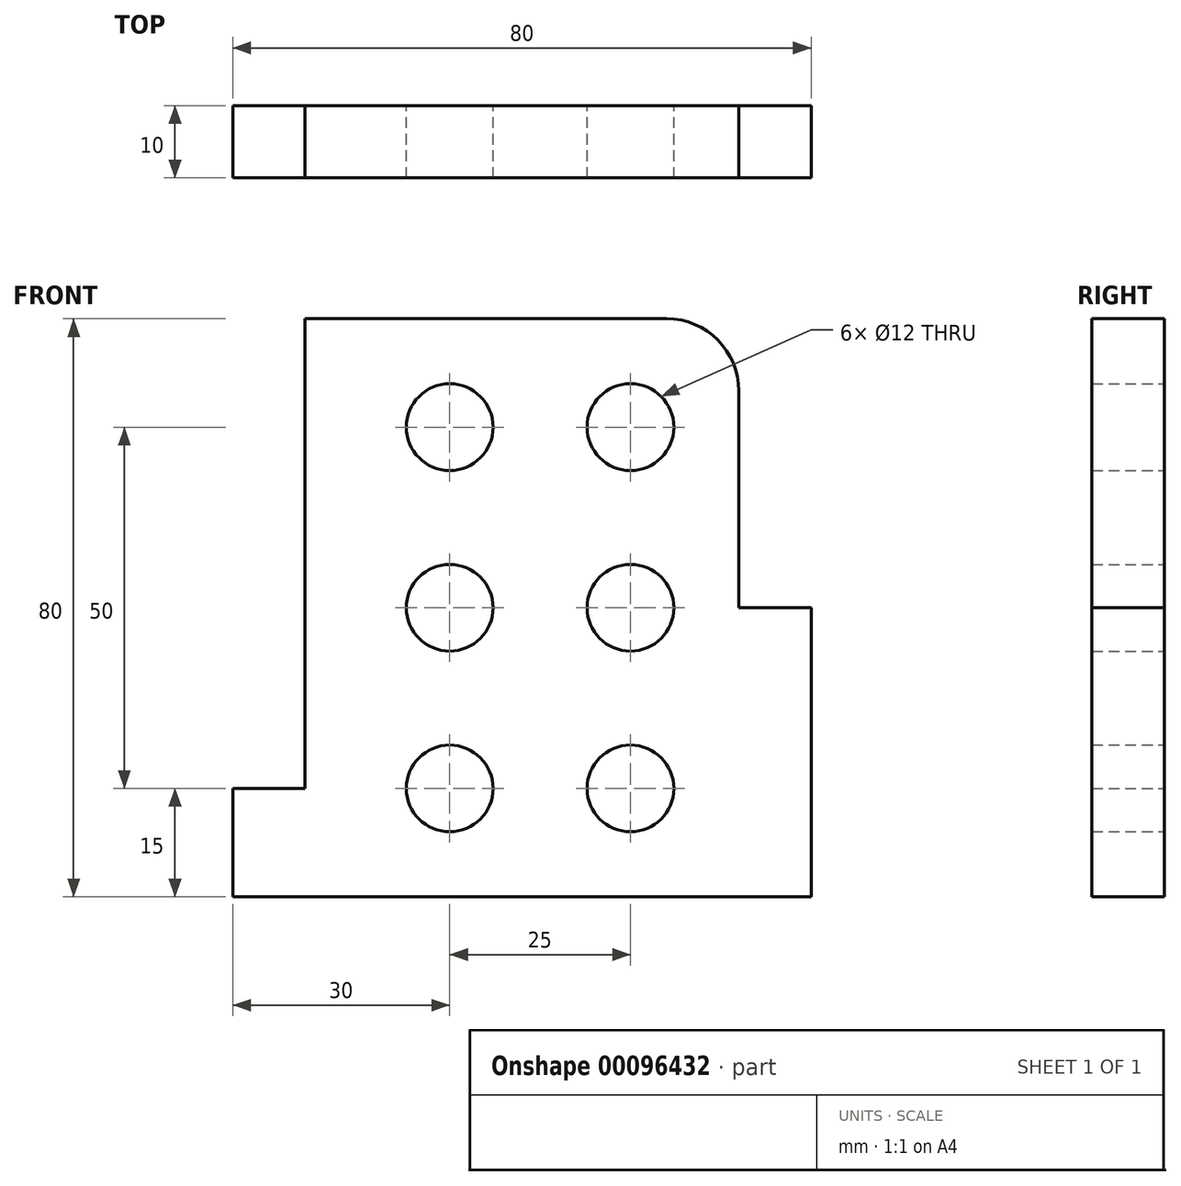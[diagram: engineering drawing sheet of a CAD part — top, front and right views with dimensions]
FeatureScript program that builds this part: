
annotation { "Feature Type Name" : "Feature", "Feature Type Description" : "" }
export const myFeature = defineFeature(function(context is Context, id is Id, definition is map)
    precondition{}
    {
        {
            var Q0;
            Q0=qCreatedBy(makeId("Front.planeOp"),FACE);
            var sketch = newSketch(context, id + "F0", { "sketchPlane" : qUnion([Q0])});
            skLineSegment(sketch, "E0", {"start": v(0, 0) * mm, "end": v(80, 0) * mm});
            skLineSegment(sketch, "E1", {"start": v(80, 0) * mm, "end": v(80, 40) * mm});
            skLineSegment(sketch, "E2", {"start": v(80, 40) * mm, "end": v(70, 40) * mm});
            skLineSegment(sketch, "E3", {"start": v(70, 40) * mm, "end": v(70, 70) * mm});
            skLineSegment(sketch, "E4", {"start": v(0, 0) * mm, "end": v(0, 15) * mm});
            skLineSegment(sketch, "E5", {"start": v(0, 15) * mm, "end": v(10, 15) * mm});
            skLineSegment(sketch, "E6", {"start": v(10, 15) * mm, "end": v(10, 80) * mm});
            skLineSegment(sketch, "E7", {"start": v(10, 80) * mm, "end": v(60, 80) * mm});
            skCircle(sketch, "E8", {"center": v(30, 15) * mm, "radius": 6 * mm});
            skCircle(sketch, "E9", {"center": v(55, 15) * mm, "radius": 6 * mm});
            skCircle(sketch, "E10", {"center": v(30, 40) * mm, "radius": 6 * mm});
            skCircle(sketch, "E11", {"center": v(55, 40) * mm, "radius": 6 * mm});
            skCircle(sketch, "E12", {"center": v(30, 65) * mm, "radius": 6 * mm});
            skCircle(sketch, "E13", {"center": v(55, 65) * mm, "radius": 6 * mm});
            skPoint(sketch, "E14.visualSharp", {"position": v(70, 80) * mm});
            skArc(sketch, "E14.filletArc", {"start": v(70, 70) * mm, "mid": v(67.07, 77.07) * mm, "end": v(60, 80) * mm});
            skSolve(sketch);
        }
        {
            var Q0;
            Q0=makeQuery(id+"F0.imprint","IMPRINT",FACE,{"disambiguationData":[TD([[makeQuery(id+"F0.imprint","IMPRINT",EDGE,{"derivedFrom":sQuery(id+"F0.wireOp",EDGE,"E0")}),1.0]])]});
            extrude(context, id + "F1", {"entities" : qUnion([Q0]), "depth" : 10 * mm});
        }
    });
